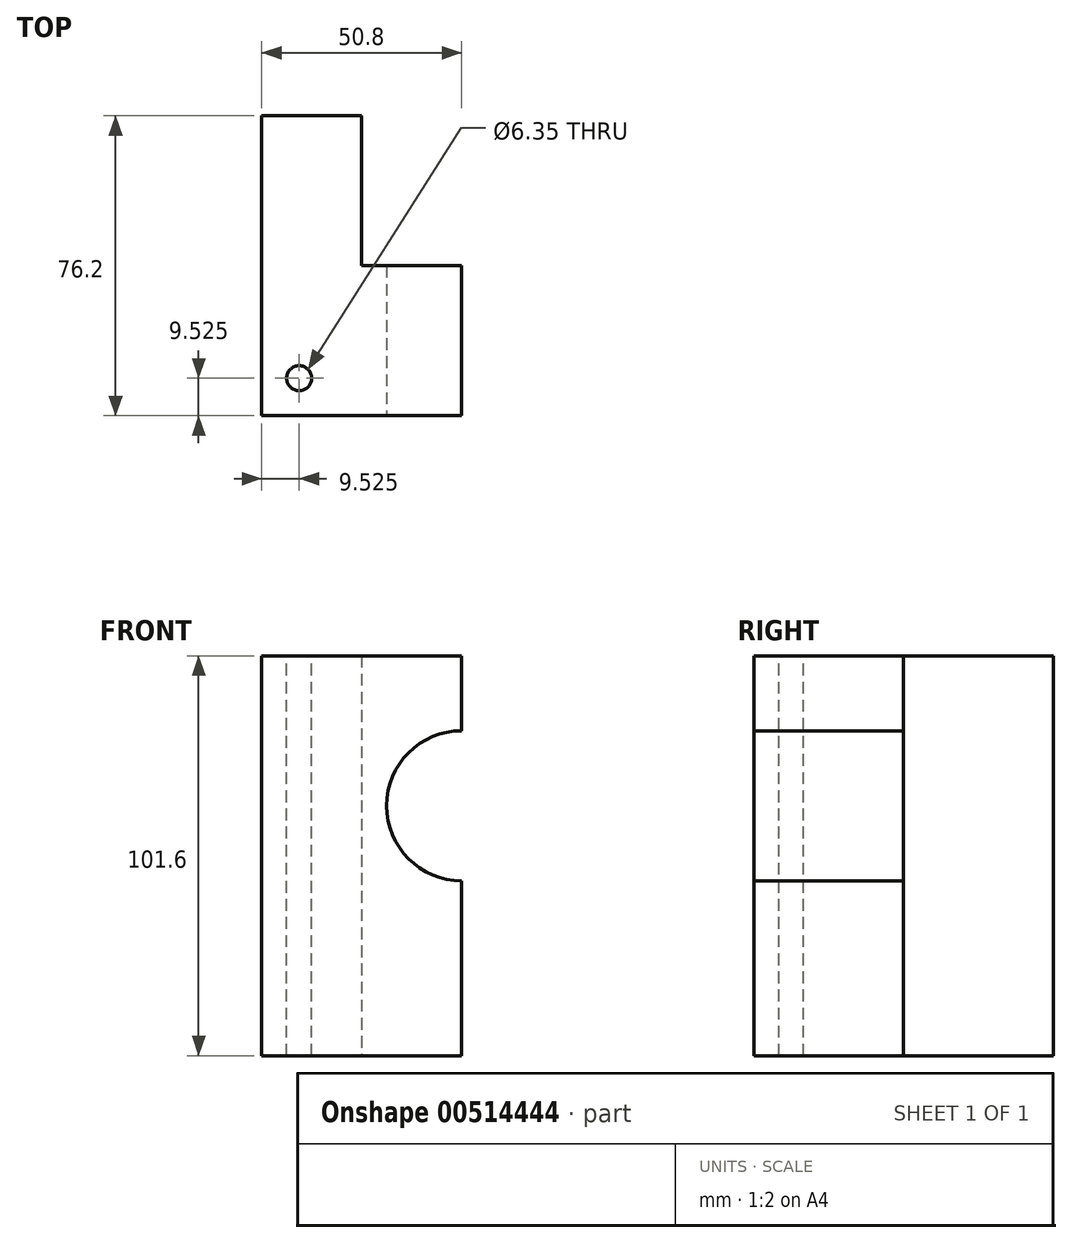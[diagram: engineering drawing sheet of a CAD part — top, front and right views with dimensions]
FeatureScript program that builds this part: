
annotation { "Feature Type Name" : "Feature", "Feature Type Description" : "" }
export const myFeature = defineFeature(function(context is Context, id is Id, definition is map)
    precondition{}
    {
        {
            var Q0;
            Q0=qCreatedBy(makeId("Top.planeOp"),FACE);
            var sketch = newSketch(context, id + "F0", { "sketchPlane" : qUnion([Q0])});
            skLineSegment(sketch, "E0.bottom", {"start": v(0, 38.1) * mm, "end": v(-25.4, 38.1) * mm});
            skLineSegment(sketch, "E0.top", {"start": v(25.4, -38.1) * mm, "end": v(-25.4, -38.1) * mm});
            skLineSegment(sketch, "E0.left", {"start": v(25.4, 0) * mm, "end": v(25.4, -38.1) * mm});
            skLineSegment(sketch, "E0.right", {"start": v(-25.4, 38.1) * mm, "end": v(-25.4, -38.1) * mm});
            skPoint(sketch, "E0.middle", {"position": v(0, 0) * mm});
            skLineSegment(sketch, "E1", {"start": v(0, 38.1) * mm, "end": v(0, 0) * mm});
            skLineSegment(sketch, "E2", {"start": v(0, 0) * mm, "end": v(25.4, 0) * mm});
            skPoint(sketch, "E3.orphan", {"position": v(25.4, 38.1) * mm});
            skSolve(sketch);
        }
        {
            var Q0;
            Q0 = qSketchRegion(id + "F0", true);
            extrude(context, id + "F1", {"entities" : qUnion([Q0]), "depth" : 101.6 * mm});
        }
        {
            var Q0;
            Q0=makeQuery(id+"F1.opExtrude","CAP_FACE",FACE,{"disambiguationData":[OSD([sQuery(id+"F0.wireOp",EDGE,"E0.bottom"),sQuery(id+"F0.wireOp",EDGE,"E0.top"),sQuery(id+"F0.wireOp",EDGE,"E0.left"),sQuery(id+"F0.wireOp",EDGE,"E0.right"),sQuery(id+"F0.wireOp",EDGE,"E1"),sQuery(id+"F0.wireOp",EDGE,"E2")])],"isStart":false});
            var sketch = newSketch(context, id + "F2", { "sketchPlane" : qUnion([Q0])});
            skCircle(sketch, "E4", {"center": v(-15.88, -28.58) * mm, "radius": 3.18 * mm});
            skSolve(sketch);
        }
        {
            var Q0;
            Q0 = qSketchRegion(id + "F2", true);
            extrude(context, id + "F3", {"entities" : qUnion([Q0]), "operationType" : NewBodyOperationType.REMOVE, "endBound" : BoundingType.UP_TO_NEXT, "oppositeDirection" : true, "depth" : 25.4 * mm});
        }
        {
            var Q0;
            Q0=makeQuery(id+"F1.opExtrude","SWEPT_FACE",FACE,{"disambiguationData":[OSD([sQuery(id+"F0.wireOp",EDGE,"E0.top")])]});
            var sketch = newSketch(context, id + "F4", { "sketchPlane" : qUnion([Q0])});
            skCircle(sketch, "E5", {"center": v(25.4, 63.5) * mm, "radius": 19.05 * mm});
            skSolve(sketch);
        }
        {
            var Q0;
            Q0 = qSketchRegion(id + "F4", true);
            extrude(context, id + "F5", {"entities" : qUnion([Q0]), "operationType" : NewBodyOperationType.REMOVE, "endBound" : BoundingType.UP_TO_NEXT, "oppositeDirection" : true, "depth" : 25.4 * mm});
        }
    });
